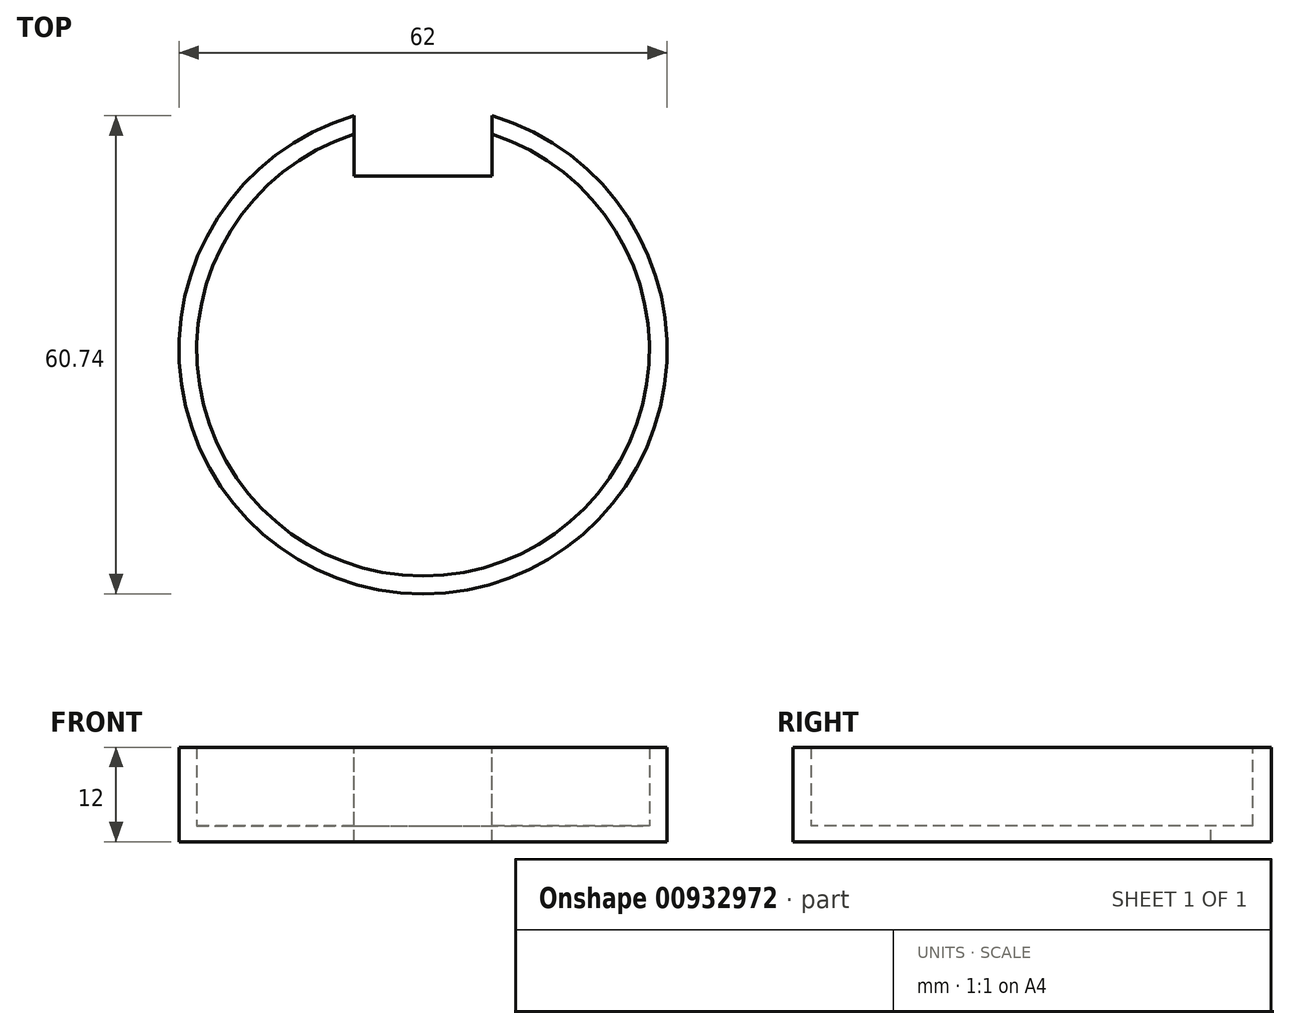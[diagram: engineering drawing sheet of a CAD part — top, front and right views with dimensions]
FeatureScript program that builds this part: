
annotation { "Feature Type Name" : "Feature", "Feature Type Description" : "" }
export const myFeature = defineFeature(function(context is Context, id is Id, definition is map)
    precondition{}
    {
        {
            var Q0;
            Q0=qCreatedBy(makeId("Top.planeOp"),FACE);
            var sketch = newSketch(context, id + "F0", { "sketchPlane" : qUnion([Q0])});
            skCircle(sketch, "E0", {"center": v(0, 0) * mm, "radius": 31 * mm});
            skCircle(sketch, "E1", {"center": v(0, 0) * mm, "radius": 28.75 * mm});
            skLineSegment(sketch, "E2.bottom", {"start": v(-8.75, 35.37) * mm, "end": v(8.75, 35.37) * mm});
            skLineSegment(sketch, "E2.top", {"start": v(-8.75, 22.1) * mm, "end": v(8.75, 22.1) * mm});
            skLineSegment(sketch, "E2.left", {"start": v(-8.75, 35.37) * mm, "end": v(-8.75, 22.1) * mm});
            skLineSegment(sketch, "E2.right", {"start": v(8.75, 35.37) * mm, "end": v(8.75, 22.1) * mm});
            skSolve(sketch);
        }
        {
            var Q0;
            Q0=makeQuery(id+"F0.imprint","IMPRINT",FACE,{"disambiguationData":[TD([[makeQuery(id+"F0.imprint","IMPRINT",EDGE,{"derivedFrom":sQuery(id+"F0.wireOp",EDGE,"E0")}),1.0]])]});
            var Q1;
            Q1=makeQuery(id+"F0.imprint","IMPRINT",FACE,{"disambiguationData":[TD([[makeQuery(id+"F0.imprint","IMPRINT",EDGE,{"derivedFrom":sQuery(id+"F0.wireOp",EDGE,"E1")}),1.0]])]});
            extrude(context, id + "F1", {"entities" : qUnion([Q0, Q1]), "depth" : -2 * mm, "offsetDistance" : 25 * mm});
        }
        {
            var Q0;
            Q0=makeQuery(id+"F0.imprint","IMPRINT",FACE,{"disambiguationData":[TD([[makeQuery(id+"F0.imprint","IMPRINT",EDGE,{"derivedFrom":sQuery(id+"F0.wireOp",EDGE,"E0")}),1.0]])]});
            extrude(context, id + "F2", {"entities" : qUnion([Q0]), "operationType" : NewBodyOperationType.ADD, "depth" : 10 * mm, "offsetDistance" : 25 * mm});
        }
        {
            var Q0;
            {var subQ5=sQuery(id+"F0.wireOp",EDGE,"E2.top");Q0=makeQuery(id+"F0.imprint","IMPRINT",FACE,{"disambiguationData":[TD([[makeQuery(id+"F0.imprint","IMPRINT",EDGE,{"derivedFrom":subQ5}),1.0]])]});}
            var Q1;
            {var subQ5=sQuery(id+"F0.wireOp",EDGE,"E2.bottom");Q1=makeQuery(id+"F0.imprint","IMPRINT",FACE,{"disambiguationData":[TD([[makeQuery(id+"F0.imprint","IMPRINT",EDGE,{"derivedFrom":subQ5}),-1.0]])]});}
            var Q2;
            {var subQ0=sQuery(id+"F0.wireOp",EDGE,"E2.left");var subQ1=sQuery(id+"F0.wireOp",EDGE,"E0");var subQ2=makeQuery(id+"F0.imprint","INTERSECT",VERTEX,{"derivedFrom":[subQ1,subQ0]});Q2=makeQuery(id+"F0.imprint","IMPRINT",FACE,{"disambiguationData":[TD([[makeQuery(id+"F0.imprint","IMPRINT",EDGE,{"disambiguationData":[TD([[subQ2,1.0]])],"derivedFrom":subQ1}),1.0]])]});}
            extrude(context, id + "F3", {"entities" : qUnion([Q0, Q1, Q2]), "operationType" : NewBodyOperationType.REMOVE, "endBound" : BoundingType.THROUGH_ALL, "oppositeDirection" : true, "depth" : 25 * mm, "offsetDistance" : 25 * mm});
        }
        {
            var Q0;
            {var subQ0=sQuery(id+"F0.wireOp",EDGE,"E2.left");var subQ1=sQuery(id+"F0.wireOp",EDGE,"E0");var subQ2=makeQuery(id+"F0.imprint","INTERSECT",VERTEX,{"derivedFrom":[subQ1,subQ0]});Q0=makeQuery(id+"F0.imprint","IMPRINT",FACE,{"disambiguationData":[TD([[makeQuery(id+"F0.imprint","IMPRINT",EDGE,{"disambiguationData":[TD([[subQ2,1.0]])],"derivedFrom":subQ1}),1.0]])]});}
            extrude(context, id + "F4", {"entities" : qUnion([Q0]), "operationType" : NewBodyOperationType.REMOVE, "oppositeDirection" : true, "depth" : 25 * mm, "offsetDistance" : 25 * mm, "hasSecondDirection" : true, "secondDirectionOppositeDirection" : false, "secondDirectionDepth" : 25 * mm});
        }
    });
